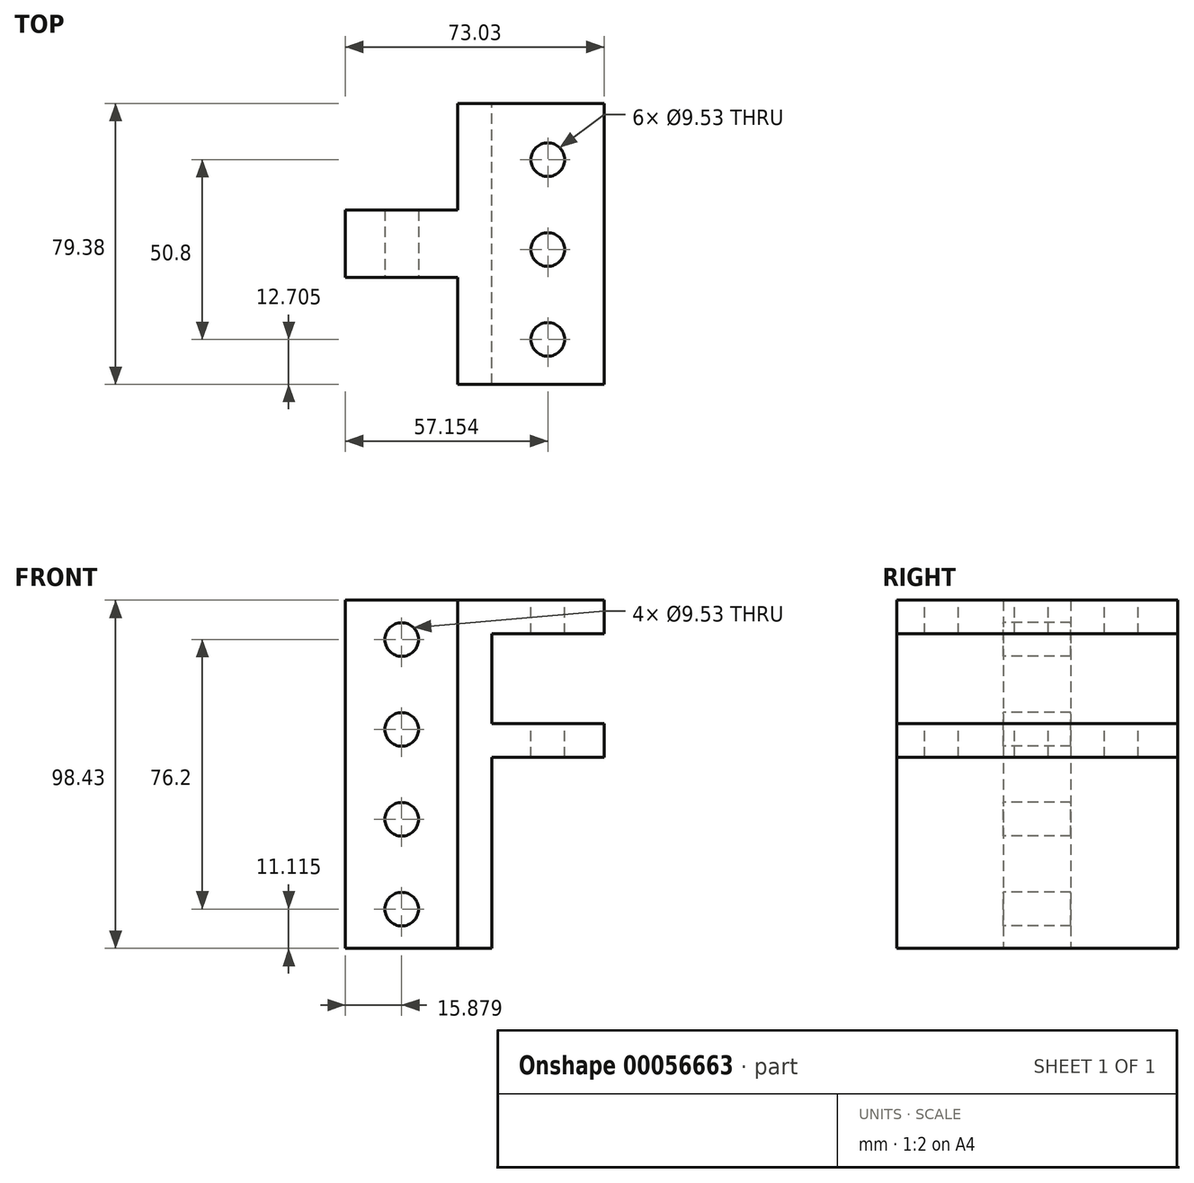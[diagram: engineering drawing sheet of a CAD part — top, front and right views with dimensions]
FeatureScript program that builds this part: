
annotation { "Feature Type Name" : "Feature", "Feature Type Description" : "" }
export const myFeature = defineFeature(function(context is Context, id is Id, definition is map)
    precondition{}
    {
        {
            var Q0;
            Q0=qCreatedBy(makeId("Front.planeOp"),FACE);
            var sketch = newSketch(context, id + "F0", { "sketchPlane" : qUnion([Q0])});
            skLineSegment(sketch, "E0", {"start": v(-39.48, -58.55) * mm, "end": v(-29.95, -58.55) * mm});
            skLineSegment(sketch, "E1", {"start": v(-29.95, -58.55) * mm, "end": v(-29.95, -4.57) * mm});
            skLineSegment(sketch, "E2", {"start": v(-29.95, -4.57) * mm, "end": v(1.8, -4.57) * mm});
            skLineSegment(sketch, "E3", {"start": v(1.8, -4.57) * mm, "end": v(1.8, 4.95) * mm});
            skLineSegment(sketch, "E4", {"start": v(1.8, 4.95) * mm, "end": v(-29.95, 4.95) * mm});
            skLineSegment(sketch, "E5", {"start": v(-29.95, 4.95) * mm, "end": v(-29.95, 30.35) * mm});
            skLineSegment(sketch, "E6", {"start": v(-29.95, 30.35) * mm, "end": v(1.8, 30.35) * mm});
            skLineSegment(sketch, "E7", {"start": v(1.8, 30.35) * mm, "end": v(1.8, 39.88) * mm});
            skLineSegment(sketch, "E8", {"start": v(1.8, 39.88) * mm, "end": v(-39.48, 39.88) * mm});
            skLineSegment(sketch, "E9", {"start": v(-39.48, 39.88) * mm, "end": v(-39.48, -58.55) * mm});
            skSolve(sketch);
        }
        {
            var Q0;
            Q0 = qSketchRegion(id + "F0", true);
            extrude(context, id + "F1", {"entities" : qUnion([Q0]), "depth" : 79.38 * mm});
        }
        {
            var Q0;
            Q0=makeQuery(id+"F1.opExtrude","SWEPT_FACE",FACE,{"disambiguationData":[OSD([sQuery(id+"F0.wireOp",EDGE,"E9")])]});
            var sketch = newSketch(context, id + "F2", { "sketchPlane" : qUnion([Q0])});
            skLineSegment(sketch, "E10.bottom", {"start": v(30.16, 39.88) * mm, "end": v(49.21, 39.88) * mm});
            skLineSegment(sketch, "E10.top", {"start": v(30.16, -58.55) * mm, "end": v(49.21, -58.55) * mm});
            skLineSegment(sketch, "E10.left", {"start": v(30.16, 39.88) * mm, "end": v(30.16, -58.55) * mm});
            skLineSegment(sketch, "E10.right", {"start": v(49.21, 39.88) * mm, "end": v(49.21, -58.55) * mm});
            skSolve(sketch);
        }
        {
            var Q0;
            Q0 = qSketchRegion(id + "F2", true);
            extrude(context, id + "F3", {"entities" : qUnion([Q0]), "operationType" : NewBodyOperationType.ADD, "depth" : 31.75 * mm});
        }
        {
            var Q0;
            Q0=makeQuery(id+"F3.opExtrude","SWEPT_FACE",FACE,{"disambiguationData":[OSD([sQuery(id+"F2.wireOp",EDGE,"E10.right")])]});
            var sketch = newSketch(context, id + "F4", { "sketchPlane" : qUnion([Q0])});
            skCircle(sketch, "E11", {"center": v(-55.35, 28.77) * mm, "radius": 4.76 * mm});
            skCircle(sketch, "E12.0.1.0", {"center": v(-55.35, 3.37) * mm, "radius": 4.76 * mm});
            skCircle(sketch, "E12.0.2.0", {"center": v(-55.35, -22.03) * mm, "radius": 4.76 * mm});
            skCircle(sketch, "E12.0.3.0", {"center": v(-55.35, -47.43) * mm, "radius": 4.76 * mm});
            skLineSegment(sketch, "E12.direction1", {"start": v(-55.35, 28.77) * mm, "end": v(-5.35, 28.77) * mm, "construction": true});
            skLineSegment(sketch, "E12.direction2", {"start": v(-55.35, 28.77) * mm, "end": v(-55.35, 3.37) * mm, "construction": true});
            skSolve(sketch);
        }
        {
            var Q0;
            Q0 = qSketchRegion(id + "F4", true);
            extrude(context, id + "F5", {"entities" : qUnion([Q0]), "operationType" : NewBodyOperationType.REMOVE, "endBound" : BoundingType.THROUGH_ALL, "oppositeDirection" : true, "depth" : 25.4 * mm});
        }
        {
            var Q0;
            Q0=makeQuery(id+"F3.boolean.opBoolean","MERGE",FACE,{"derivedFrom":[makeQuery(id+"F1.opExtrude","SWEPT_FACE",FACE,{"disambiguationData":[OSD([sQuery(id+"F0.wireOp",EDGE,"E8")])]}),makeQuery(id+"F3.opExtrude","SWEPT_FACE",FACE,{"disambiguationData":[OSD([sQuery(id+"F2.wireOp",EDGE,"E10.bottom")])]})]});
            var sketch = newSketch(context, id + "F6", { "sketchPlane" : qUnion([Q0])});
            skCircle(sketch, "E13", {"center": v(-14.08, -15.88) * mm, "radius": 4.76 * mm});
            skCircle(sketch, "E14.0.1.0", {"center": v(-14.08, -41.27) * mm, "radius": 4.76 * mm});
            skCircle(sketch, "E14.0.2.0", {"center": v(-14.08, -66.67) * mm, "radius": 4.76 * mm});
            skLineSegment(sketch, "E14.direction1", {"start": v(-14.08, -15.88) * mm, "end": v(35.92, -15.88) * mm, "construction": true});
            skLineSegment(sketch, "E14.direction2", {"start": v(-14.08, -15.88) * mm, "end": v(-14.08, -41.27) * mm, "construction": true});
            skSolve(sketch);
        }
        {
            var Q0;
            Q0 = qSketchRegion(id + "F6", true);
            extrude(context, id + "F7", {"entities" : qUnion([Q0]), "operationType" : NewBodyOperationType.REMOVE, "endBound" : BoundingType.THROUGH_ALL, "oppositeDirection" : true, "depth" : 25.4 * mm});
        }
    });
